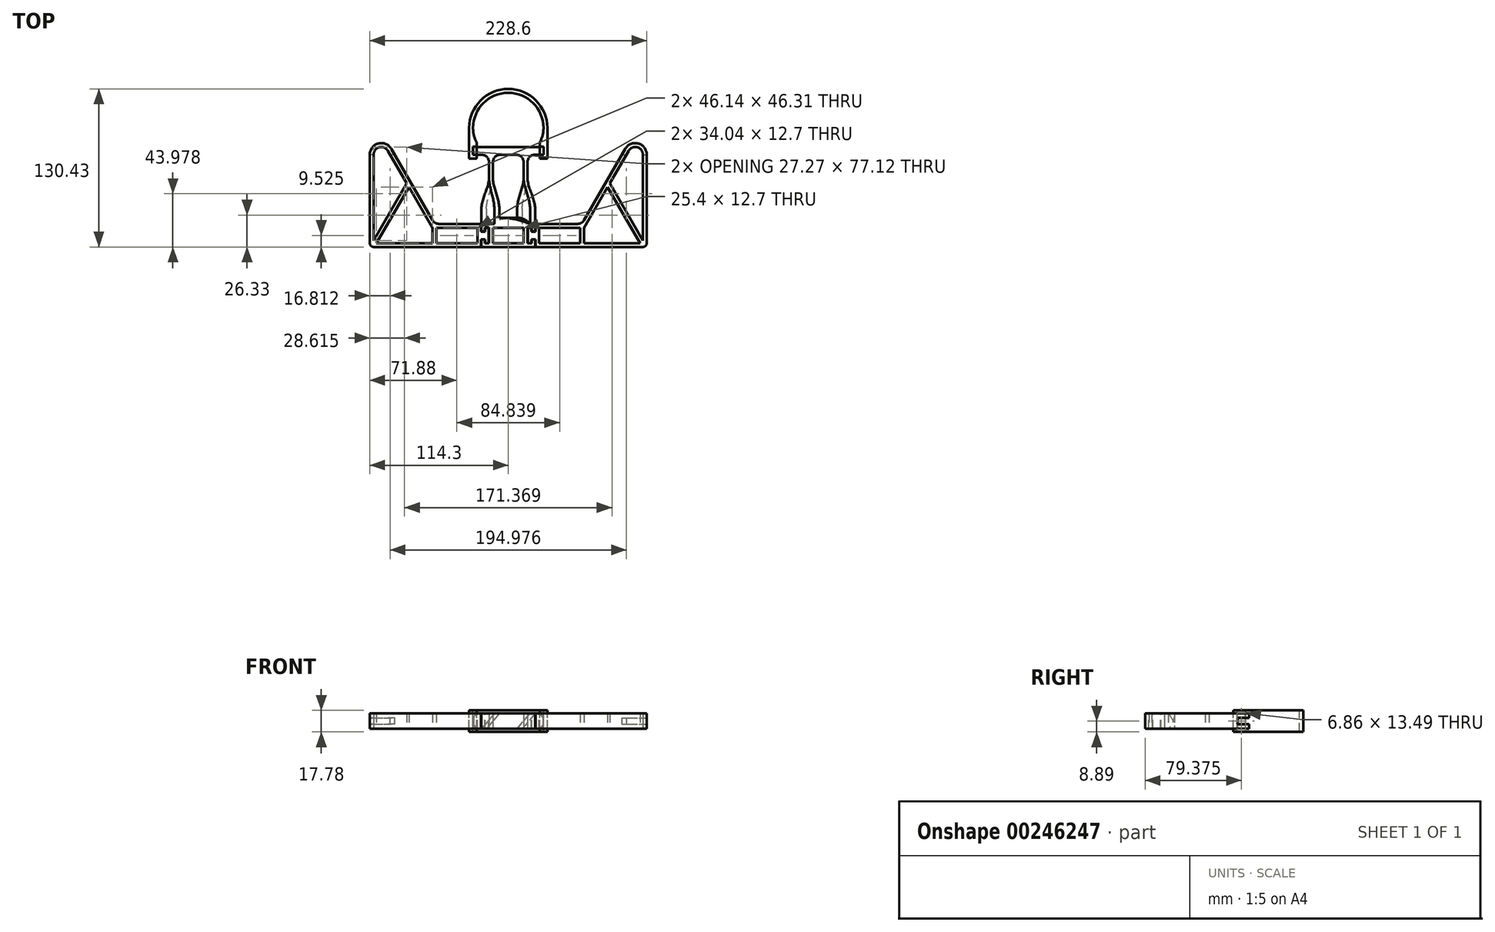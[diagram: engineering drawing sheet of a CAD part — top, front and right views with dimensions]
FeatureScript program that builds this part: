
annotation { "Feature Type Name" : "Feature", "Feature Type Description" : "" }
export const myFeature = defineFeature(function(context is Context, id is Id, definition is map)
    precondition{}
    {
        {
            var Q0;
            Q0=qCreatedBy(makeId("Top.planeOp"),FACE);
            var sketch = newSketch(context, id + "F0", { "sketchPlane" : qUnion([Q0])});
            skLineSegment(sketch, "E0", {"start": v(0, 0) * mm, "end": v(111.12, 0) * mm});
            skLineSegment(sketch, "E1", {"start": v(114.3, 3.18) * mm, "end": v(114.3, 76.2) * mm});
            skLineSegment(sketch, "E2", {"start": v(108.76, 3.18) * mm, "end": v(62.61, 3.18) * mm});
            skLineSegment(sketch, "E3", {"start": v(62.61, 3.18) * mm, "end": v(62.61, 15.88) * mm});
            skLineSegment(sketch, "E4", {"start": v(60.78, 19.05) * mm, "end": v(15.88, 19.05) * mm});
            skLineSegment(sketch, "E5", {"start": v(15.88, 19.05) * mm, "end": v(15.88, 76.2) * mm});
            skLineSegment(sketch, "E6", {"start": v(15.87, 76.2) * mm, "end": v(28.58, 76.2) * mm});
            skLineSegment(sketch, "E7", {"start": v(28.58, 76.2) * mm, "end": v(28.58, 82.55) * mm});
            skLineSegment(sketch, "E8", {"start": v(28.58, 82.55) * mm, "end": v(-28.58, 82.55) * mm});
            skLineSegment(sketch, "E9", {"start": v(-28.58, 82.55) * mm, "end": v(-28.58, 76.2) * mm});
            skLineSegment(sketch, "E10", {"start": v(-28.58, 76.2) * mm, "end": v(-15.87, 76.2) * mm});
            skLineSegment(sketch, "E11", {"start": v(-15.87, 76.2) * mm, "end": v(-15.88, 19.05) * mm});
            skLineSegment(sketch, "E12.bottom", {"start": v(59.44, 15.88) * mm, "end": v(0, 15.88) * mm});
            skLineSegment(sketch, "E12.top", {"start": v(59.44, 3.18) * mm, "end": v(0, 3.18) * mm});
            skLineSegment(sketch, "E12.left", {"start": v(59.44, 15.88) * mm, "end": v(59.44, 3.18) * mm});
            skPoint(sketch, "E13", {"position": v(0, 82.55) * mm});
            skLineSegment(sketch, "E14", {"start": v(-15.88, 76.2) * mm, "end": v(15.87, 76.2) * mm, "construction": true});
            skPoint(sketch, "E15", {"position": v(0, 76.2) * mm});
            skArc(sketch, "E16", {"start": v(111.13, 76.2) * mm, "mid": v(106.42, 82.33) * mm, "end": v(99.28, 79.38) * mm});
            skLineSegment(sketch, "E17", {"start": v(111.13, 5.42) * mm, "end": v(111.13, 76.2) * mm});
            skPoint(sketch, "E18.visualSharp", {"position": v(111.13, 3.18) * mm});
            skPoint(sketch, "E19.visualSharp", {"position": v(114.3, 0) * mm});
            skArc(sketch, "E19.filletArc", {"start": v(111.13, 0) * mm, "mid": v(113.37, 0.93) * mm, "end": v(114.3, 3.18) * mm});
            skLineSegment(sketch, "E20", {"start": v(108.76, 3.17) * mm, "end": v(82.02, 49.48) * mm});
            skLineSegment(sketch, "E21", {"start": v(111.13, 5.42) * mm, "end": v(83.85, 52.66) * mm});
            skLineSegment(sketch, "E22", {"start": v(0, 3.18) * mm, "end": v(0, 15.88) * mm, "construction": true});
            skArc(sketch, "E23", {"start": v(114.3, 76.2) * mm, "mid": v(107.24, 85.4) * mm, "end": v(96.53, 80.96) * mm});
            skLineSegment(sketch, "E24", {"start": v(96.53, 80.96) * mm, "end": v(60.78, 19.05) * mm});
            skLineSegment(sketch, "E25", {"start": v(99.28, 79.38) * mm, "end": v(83.85, 52.66) * mm});
            skLineSegment(sketch, "E26.trimOffspring", {"start": v(82.02, 49.48) * mm, "end": v(62.61, 15.88) * mm});
            skLineSegment(sketch, "E27.bottom", {"start": v(12.7, 19.05) * mm, "end": v(-12.7, 19.05) * mm});
            skLineSegment(sketch, "E27.top", {"start": v(12.7, 76.2) * mm, "end": v(-12.7, 76.2) * mm});
            skLineSegment(sketch, "E27.left", {"start": v(12.7, 19.05) * mm, "end": v(12.7, 76.2) * mm});
            skLineSegment(sketch, "E27.right", {"start": v(-12.7, 19.05) * mm, "end": v(-12.7, 76.2) * mm});
            skLineSegment(sketch, "E28.MirrorCS", {"start": v(-60.78, 19.05) * mm, "end": v(-15.88, 19.05) * mm});
            skLineSegment(sketch, "E29.MirrorCS", {"start": v(-59.44, 15.88) * mm, "end": v(0, 15.88) * mm});
            skLineSegment(sketch, "E30.MirrorCS", {"start": v(-59.44, 3.18) * mm, "end": v(0, 3.18) * mm});
            skLineSegment(sketch, "E31.MirrorCS", {"start": v(0, 0) * mm, "end": v(-111.12, 0) * mm});
            skLineSegment(sketch, "E32.MirrorCS", {"start": v(-59.44, 15.88) * mm, "end": v(-59.44, 3.18) * mm});
            skLineSegment(sketch, "E33.MirrorCS", {"start": v(-62.61, 3.18) * mm, "end": v(-62.61, 15.88) * mm});
            skLineSegment(sketch, "E34.MirrorCS", {"start": v(-82.02, 49.48) * mm, "end": v(-62.61, 15.88) * mm});
            skLineSegment(sketch, "E35.MirrorCS", {"start": v(-96.53, 80.96) * mm, "end": v(-60.78, 19.05) * mm});
            skArc(sketch, "E36.MirrorCS", {"start": v(-114.3, 76.2) * mm, "mid": v(-107.24, 85.4) * mm, "end": v(-96.53, 80.96) * mm});
            skArc(sketch, "E37.MirrorCS", {"start": v(-111.13, 76.2) * mm, "mid": v(-106.42, 82.33) * mm, "end": v(-99.28, 79.38) * mm});
            skLineSegment(sketch, "E38.MirrorCS", {"start": v(-99.28, 79.38) * mm, "end": v(-83.85, 52.66) * mm});
            skLineSegment(sketch, "E39.MirrorCS", {"start": v(-111.13, 5.42) * mm, "end": v(-83.85, 52.66) * mm});
            skLineSegment(sketch, "E40.MirrorCS", {"start": v(-108.76, 3.17) * mm, "end": v(-82.02, 49.48) * mm});
            skArc(sketch, "E41.MirrorCS", {"start": v(-111.13, 0) * mm, "mid": v(-113.37, 0.93) * mm, "end": v(-114.3, 3.18) * mm});
            skLineSegment(sketch, "E42.MirrorCS", {"start": v(-114.3, 3.18) * mm, "end": v(-114.3, 76.2) * mm});
            skLineSegment(sketch, "E43.MirrorCS", {"start": v(-111.13, 5.42) * mm, "end": v(-111.13, 76.2) * mm});
            skLineSegment(sketch, "E44.MirrorCS", {"start": v(-108.76, 3.18) * mm, "end": v(-62.61, 3.18) * mm});
            skSolve(sketch);
        }
        {
            var Q0;
            Q0=makeQuery(id+"F0.imprint","IMPRINT",FACE,{"disambiguationData":[TD([[makeQuery(id+"F0.imprint","IMPRINT",EDGE,{"derivedFrom":sQuery(id+"F0.wireOp",EDGE,"E0")}),1.0]])]});
            extrude(context, id + "F1", {"entities" : qUnion([Q0]), "depth" : 12.7 * mm});
        }
        {
            var Q0;
            Q0=makeQuery(id+"F1.opExtrude","CAP_EDGE",EDGE,{"disambiguationData":[OSD([sQuery(id+"F0.wireOp",EDGE,"E7")])],"isStart":true});
            var Q1;
            Q1=makeQuery(id+"F1.opExtrude","CAP_EDGE",EDGE,{"disambiguationData":[OSD([sQuery(id+"F0.wireOp",EDGE,"E7")])],"isStart":false});
            chamfer(context, id + "F2", {"entities" : qUnion([Q0, Q1]), "chamferType" : ChamferType.OFFSET_ANGLE, "width" : 3.17 * mm, "oppositeDirection" : false, "angle" : 40 * degree, "tangentPropagation" : true});
        }
        {
            var Q0;
            Q0=makeQuery(id+"F1.opExtrude","CAP_EDGE",EDGE,{"disambiguationData":[OSD([sQuery(id+"F0.wireOp",EDGE,"E9")])],"isStart":false});
            var Q1;
            Q1=makeQuery(id+"F1.opExtrude","CAP_EDGE",EDGE,{"disambiguationData":[OSD([sQuery(id+"F0.wireOp",EDGE,"E9")])],"isStart":true});
            chamfer(context, id + "F3", {"entities" : qUnion([Q0, Q1]), "chamferType" : ChamferType.OFFSET_ANGLE, "width" : 3.17 * mm, "oppositeDirection" : true, "angle" : 40 * degree, "tangentPropagation" : true});
        }
        {
            var Q0;
            Q0=makeQuery(id+"F1.opExtrude","SWEPT_EDGE",EDGE,{"disambiguationData":[OSD([sQuery(id+"F0.wireOp",EDGE,"E4"),sQuery(id+"F0.wireOp",EDGE,"E24")])]});
            var Q1;
            Q1=makeQuery(id+"F1.opExtrude","SWEPT_EDGE",EDGE,{"disambiguationData":[OSD([sQuery(id+"F0.wireOp",EDGE,"E5"),sQuery(id+"F0.wireOp",EDGE,"E6")])]});
            var Q2;
            Q2=makeQuery(id+"F1.opExtrude","SWEPT_EDGE",EDGE,{"disambiguationData":[OSD([sQuery(id+"F0.wireOp",EDGE,"E10"),sQuery(id+"F0.wireOp",EDGE,"E11")])]});
            var Q3;
            Q3=makeQuery(id+"F1.opExtrude","SWEPT_EDGE",EDGE,{"disambiguationData":[OSD([sQuery(id+"F0.wireOp",EDGE,"E28.MirrorCS"),sQuery(id+"F0.wireOp",EDGE,"E35.MirrorCS")])]});
            var Q4;
            Q4=makeQuery(id+"F1.opExtrude","SWEPT_EDGE",EDGE,{"disambiguationData":[OSD([sQuery(id+"F0.wireOp",EDGE,"E27.top"),sQuery(id+"F0.wireOp",EDGE,"E27.left")])]});
            var Q5;
            Q5=makeQuery(id+"F1.opExtrude","SWEPT_EDGE",EDGE,{"disambiguationData":[OSD([sQuery(id+"F0.wireOp",EDGE,"E27.top"),sQuery(id+"F0.wireOp",EDGE,"E27.right")])]});
            fillet(context, id + "F4", {"entities" : qUnion([Q0, Q1, Q2, Q3, Q4, Q5]), "radius" : 6.35 * mm, "tangentPropagation" : true, "allowEdgeOverflow" : false});
        }
        {
            var Q0;
            Q0=makeQuery(id+"F1.opExtrude","CAP_FACE",FACE,{"disambiguationData":[OSD([sQuery(id+"F0.wireOp",EDGE,"E0"),sQuery(id+"F0.wireOp",EDGE,"E1"),sQuery(id+"F0.wireOp",EDGE,"E2"),sQuery(id+"F0.wireOp",EDGE,"E3"),sQuery(id+"F0.wireOp",EDGE,"E4"),sQuery(id+"F0.wireOp",EDGE,"E5"),sQuery(id+"F0.wireOp",EDGE,"E6"),sQuery(id+"F0.wireOp",EDGE,"E7"),sQuery(id+"F0.wireOp",EDGE,"E8"),sQuery(id+"F0.wireOp",EDGE,"E9"),sQuery(id+"F0.wireOp",EDGE,"E10"),sQuery(id+"F0.wireOp",EDGE,"E11"),sQuery(id+"F0.wireOp",EDGE,"E12.bottom"),sQuery(id+"F0.wireOp",EDGE,"E12.top"),sQuery(id+"F0.wireOp",EDGE,"E12.left"),sQuery(id+"F0.wireOp",EDGE,"E16"),sQuery(id+"F0.wireOp",EDGE,"E17"),sQuery(id+"F0.wireOp",EDGE,"E19.filletArc"),sQuery(id+"F0.wireOp",EDGE,"E20"),sQuery(id+"F0.wireOp",EDGE,"E21"),sQuery(id+"F0.wireOp",EDGE,"E23"),sQuery(id+"F0.wireOp",EDGE,"E24"),sQuery(id+"F0.wireOp",EDGE,"E25"),sQuery(id+"F0.wireOp",EDGE,"E26.trimOffspring"),sQuery(id+"F0.wireOp",EDGE,"E27.bottom"),sQuery(id+"F0.wireOp",EDGE,"E27.top"),sQuery(id+"F0.wireOp",EDGE,"E27.left"),sQuery(id+"F0.wireOp",EDGE,"E27.right"),sQuery(id+"F0.wireOp",EDGE,"E28.MirrorCS"),sQuery(id+"F0.wireOp",EDGE,"E29.MirrorCS"),sQuery(id+"F0.wireOp",EDGE,"E30.MirrorCS"),sQuery(id+"F0.wireOp",EDGE,"E31.MirrorCS"),sQuery(id+"F0.wireOp",EDGE,"E32.MirrorCS"),sQuery(id+"F0.wireOp",EDGE,"E33.MirrorCS"),sQuery(id+"F0.wireOp",EDGE,"E34.MirrorCS"),sQuery(id+"F0.wireOp",EDGE,"E35.MirrorCS"),sQuery(id+"F0.wireOp",EDGE,"E36.MirrorCS"),sQuery(id+"F0.wireOp",EDGE,"E37.MirrorCS"),sQuery(id+"F0.wireOp",EDGE,"E38.MirrorCS"),sQuery(id+"F0.wireOp",EDGE,"E39.MirrorCS"),sQuery(id+"F0.wireOp",EDGE,"E40.MirrorCS"),sQuery(id+"F0.wireOp",EDGE,"E41.MirrorCS"),sQuery(id+"F0.wireOp",EDGE,"E42.MirrorCS"),sQuery(id+"F0.wireOp",EDGE,"E43.MirrorCS"),sQuery(id+"F0.wireOp",EDGE,"E44.MirrorCS")])],"isStart":false});
            var sketch = newSketch(context, id + "F5", { "sketchPlane" : qUnion([Q0])});
            skLineSegment(sketch, "E45.bottom", {"start": v(-25.4, 19.05) * mm, "end": v(-9.53, 19.05) * mm});
            skLineSegment(sketch, "E45.top", {"start": v(-25.4, 0) * mm, "end": v(-9.53, 0) * mm});
            skLineSegment(sketch, "E45.left", {"start": v(-25.4, 19.05) * mm, "end": v(-25.4, 0) * mm});
            skLineSegment(sketch, "E45.right", {"start": v(-9.53, 19.05) * mm, "end": v(-9.53, 0) * mm});
            skLineSegment(sketch, "E46.bottom", {"start": v(25.4, 19.05) * mm, "end": v(9.52, 19.05) * mm});
            skLineSegment(sketch, "E46.top", {"start": v(25.4, 0) * mm, "end": v(9.53, 0) * mm});
            skLineSegment(sketch, "E46.left", {"start": v(25.4, 19.05) * mm, "end": v(25.4, 0) * mm});
            skLineSegment(sketch, "E46.right", {"start": v(9.52, 19.05) * mm, "end": v(9.53, 0) * mm});
            skSolve(sketch);
        }
        {
            var Q0;
            {var subQ0=sQuery(id+"F5.wireOp",EDGE,"E45.left");var subQ1=makeQuery(id+"F1.opExtrude","CAP_EDGE",EDGE,{"disambiguationData":[OSD([sQuery(id+"F0.wireOp",EDGE,"E12.bottom"),sQuery(id+"F0.wireOp",EDGE,"E29.MirrorCS")])],"isStart":false});var subQ2=makeQuery(id+"F5.imprint","INTERSECT",VERTEX,{"derivedFrom":[subQ1,subQ0]});Q0=makeQuery(id+"F5.imprint","IMPRINT",FACE,{"disambiguationData":[TD([[makeQuery(id+"F5.imprint","IMPRINT",EDGE,{"disambiguationData":[TD([[subQ2,-1.0]])],"derivedFrom":subQ0}),1.0]])]});}
            var Q1;
            {var subQ0=sQuery(id+"F5.wireOp",EDGE,"E46.left");var subQ1=makeQuery(id+"F1.opExtrude","CAP_EDGE",EDGE,{"disambiguationData":[OSD([sQuery(id+"F0.wireOp",EDGE,"E12.bottom"),sQuery(id+"F0.wireOp",EDGE,"E29.MirrorCS")])],"isStart":false});var subQ2=makeQuery(id+"F5.imprint","INTERSECT",VERTEX,{"derivedFrom":[subQ1,subQ0]});Q1=makeQuery(id+"F5.imprint","IMPRINT",FACE,{"disambiguationData":[TD([[makeQuery(id+"F5.imprint","IMPRINT",EDGE,{"disambiguationData":[TD([[subQ2,-1.0]])],"derivedFrom":subQ0}),-1.0]])]});}
            var Q2;
            {var subQ0=sQuery(id+"F5.wireOp",EDGE,"E45.right");var subQ1=makeQuery(id+"F1.opExtrude","CAP_EDGE",EDGE,{"disambiguationData":[OSD([sQuery(id+"F0.wireOp",EDGE,"E12.bottom"),sQuery(id+"F0.wireOp",EDGE,"E29.MirrorCS")])],"isStart":false});var subQ2=makeQuery(id+"F5.imprint","INTERSECT",VERTEX,{"derivedFrom":[subQ1,subQ0]});Q2=makeQuery(id+"F5.imprint","IMPRINT",FACE,{"disambiguationData":[TD([[makeQuery(id+"F5.imprint","IMPRINT",EDGE,{"disambiguationData":[TD([[subQ2,-1.0]])],"derivedFrom":subQ0}),1.0]])]});}
            var Q3;
            Q3=makeQuery(id+"F1.opExtrude","CAP_FACE",FACE,{"disambiguationData":[OSD([sQuery(id+"F0.wireOp",EDGE,"E0"),sQuery(id+"F0.wireOp",EDGE,"E1"),sQuery(id+"F0.wireOp",EDGE,"E2"),sQuery(id+"F0.wireOp",EDGE,"E3"),sQuery(id+"F0.wireOp",EDGE,"E4"),sQuery(id+"F0.wireOp",EDGE,"E5"),sQuery(id+"F0.wireOp",EDGE,"E6"),sQuery(id+"F0.wireOp",EDGE,"E7"),sQuery(id+"F0.wireOp",EDGE,"E8"),sQuery(id+"F0.wireOp",EDGE,"E9"),sQuery(id+"F0.wireOp",EDGE,"E10"),sQuery(id+"F0.wireOp",EDGE,"E11"),sQuery(id+"F0.wireOp",EDGE,"E12.bottom"),sQuery(id+"F0.wireOp",EDGE,"E12.top"),sQuery(id+"F0.wireOp",EDGE,"E12.left"),sQuery(id+"F0.wireOp",EDGE,"E16"),sQuery(id+"F0.wireOp",EDGE,"E17"),sQuery(id+"F0.wireOp",EDGE,"E19.filletArc"),sQuery(id+"F0.wireOp",EDGE,"E20"),sQuery(id+"F0.wireOp",EDGE,"E21"),sQuery(id+"F0.wireOp",EDGE,"E23"),sQuery(id+"F0.wireOp",EDGE,"E24"),sQuery(id+"F0.wireOp",EDGE,"E25"),sQuery(id+"F0.wireOp",EDGE,"E26.trimOffspring"),sQuery(id+"F0.wireOp",EDGE,"E27.bottom"),sQuery(id+"F0.wireOp",EDGE,"E27.top"),sQuery(id+"F0.wireOp",EDGE,"E27.left"),sQuery(id+"F0.wireOp",EDGE,"E27.right"),sQuery(id+"F0.wireOp",EDGE,"E28.MirrorCS"),sQuery(id+"F0.wireOp",EDGE,"E29.MirrorCS"),sQuery(id+"F0.wireOp",EDGE,"E30.MirrorCS"),sQuery(id+"F0.wireOp",EDGE,"E31.MirrorCS"),sQuery(id+"F0.wireOp",EDGE,"E32.MirrorCS"),sQuery(id+"F0.wireOp",EDGE,"E33.MirrorCS"),sQuery(id+"F0.wireOp",EDGE,"E34.MirrorCS"),sQuery(id+"F0.wireOp",EDGE,"E35.MirrorCS"),sQuery(id+"F0.wireOp",EDGE,"E36.MirrorCS"),sQuery(id+"F0.wireOp",EDGE,"E37.MirrorCS"),sQuery(id+"F0.wireOp",EDGE,"E38.MirrorCS"),sQuery(id+"F0.wireOp",EDGE,"E39.MirrorCS"),sQuery(id+"F0.wireOp",EDGE,"E40.MirrorCS"),sQuery(id+"F0.wireOp",EDGE,"E41.MirrorCS"),sQuery(id+"F0.wireOp",EDGE,"E42.MirrorCS"),sQuery(id+"F0.wireOp",EDGE,"E43.MirrorCS"),sQuery(id+"F0.wireOp",EDGE,"E44.MirrorCS")])],"isStart":true});
            extrude(context, id + "F6", {"entities" : qUnion([Q0, Q1, Q2]), "operationType" : NewBodyOperationType.ADD, "endBound" : BoundingType.UP_TO_SURFACE, "oppositeDirection" : true, "endBoundEntityFace" : qUnion([Q3]), "depth" : 25.4 * mm});
        }
        {
            var Q0;
            {var subQ0=sQuery(id+"F0.wireOp",EDGE,"E30.MirrorCS");var subQ1=sQuery(id+"F0.wireOp",EDGE,"E29.MirrorCS");var subQ2=sQuery(id+"F0.wireOp",EDGE,"E12.top");var subQ3=sQuery(id+"F0.wireOp",EDGE,"E12.bottom");Q0=makeQuery(id+"F6.boolean.opBoolean","MERGE",FACE,{"derivedFrom":[makeQuery(id+"F1.opExtrude","CAP_FACE",FACE,{"disambiguationData":[OSD([sQuery(id+"F0.wireOp",EDGE,"E0"),sQuery(id+"F0.wireOp",EDGE,"E1"),sQuery(id+"F0.wireOp",EDGE,"E2"),sQuery(id+"F0.wireOp",EDGE,"E3"),sQuery(id+"F0.wireOp",EDGE,"E4"),sQuery(id+"F0.wireOp",EDGE,"E5"),sQuery(id+"F0.wireOp",EDGE,"E6"),sQuery(id+"F0.wireOp",EDGE,"E7"),sQuery(id+"F0.wireOp",EDGE,"E8"),sQuery(id+"F0.wireOp",EDGE,"E9"),sQuery(id+"F0.wireOp",EDGE,"E10"),sQuery(id+"F0.wireOp",EDGE,"E11"),subQ3,subQ2,sQuery(id+"F0.wireOp",EDGE,"E12.left"),sQuery(id+"F0.wireOp",EDGE,"E16"),sQuery(id+"F0.wireOp",EDGE,"E17"),sQuery(id+"F0.wireOp",EDGE,"E19.filletArc"),sQuery(id+"F0.wireOp",EDGE,"E20"),sQuery(id+"F0.wireOp",EDGE,"E21"),sQuery(id+"F0.wireOp",EDGE,"E23"),sQuery(id+"F0.wireOp",EDGE,"E24"),sQuery(id+"F0.wireOp",EDGE,"E25"),sQuery(id+"F0.wireOp",EDGE,"E26.trimOffspring"),sQuery(id+"F0.wireOp",EDGE,"E27.bottom"),sQuery(id+"F0.wireOp",EDGE,"E27.top"),sQuery(id+"F0.wireOp",EDGE,"E27.left"),sQuery(id+"F0.wireOp",EDGE,"E27.right"),sQuery(id+"F0.wireOp",EDGE,"E28.MirrorCS"),subQ1,subQ0,sQuery(id+"F0.wireOp",EDGE,"E31.MirrorCS"),sQuery(id+"F0.wireOp",EDGE,"E32.MirrorCS"),sQuery(id+"F0.wireOp",EDGE,"E33.MirrorCS"),sQuery(id+"F0.wireOp",EDGE,"E34.MirrorCS"),sQuery(id+"F0.wireOp",EDGE,"E35.MirrorCS"),sQuery(id+"F0.wireOp",EDGE,"E36.MirrorCS"),sQuery(id+"F0.wireOp",EDGE,"E37.MirrorCS"),sQuery(id+"F0.wireOp",EDGE,"E38.MirrorCS"),sQuery(id+"F0.wireOp",EDGE,"E39.MirrorCS"),sQuery(id+"F0.wireOp",EDGE,"E40.MirrorCS"),sQuery(id+"F0.wireOp",EDGE,"E41.MirrorCS"),sQuery(id+"F0.wireOp",EDGE,"E42.MirrorCS"),sQuery(id+"F0.wireOp",EDGE,"E43.MirrorCS"),sQuery(id+"F0.wireOp",EDGE,"E44.MirrorCS")])],"isStart":false}),makeQuery(id+"F6.opExtrude","CAP_FACE",FACE,{"disambiguationData":[OSD([subQ3,subQ2,subQ1,subQ0,sQuery(id+"F5.wireOp",EDGE,"E45.left"),sQuery(id+"F5.wireOp",EDGE,"E46.left")])],"isStart":true})]});}
            var sketch = newSketch(context, id + "F7", { "sketchPlane" : qUnion([Q0])});
            skLineSegment(sketch, "E47", {"start": v(-22.43, 19.05) * mm, "end": v(-22.43, 12.7) * mm});
            skLineSegment(sketch, "E48", {"start": v(-22.43, 12.7) * mm, "end": v(-19.05, 12.7) * mm});
            skLineSegment(sketch, "E49", {"start": v(-19.05, 12.7) * mm, "end": v(-19.05, 15.87) * mm});
            skLineSegment(sketch, "E50", {"start": v(-19.05, 15.88) * mm, "end": v(-16.08, 15.88) * mm});
            skLineSegment(sketch, "E51", {"start": v(-16.08, 15.87) * mm, "end": v(-16.08, 3.17) * mm});
            skLineSegment(sketch, "E52", {"start": v(-16.08, 3.17) * mm, "end": v(-19.05, 3.17) * mm});
            skLineSegment(sketch, "E53", {"start": v(-19.05, 3.17) * mm, "end": v(-19.05, 6.35) * mm});
            skLineSegment(sketch, "E54", {"start": v(-19.05, 6.35) * mm, "end": v(-22.43, 6.35) * mm});
            skLineSegment(sketch, "E55", {"start": v(-22.43, 6.35) * mm, "end": v(-22.43, 0) * mm});
            skLineSegment(sketch, "E56.0", {"start": v(-22.23, 6.15) * mm, "end": v(-22.22, 0) * mm});
            skLineSegment(sketch, "E56.1", {"start": v(-19.25, 6.15) * mm, "end": v(-22.23, 6.15) * mm});
            skLineSegment(sketch, "E56.2", {"start": v(-19.25, 2.97) * mm, "end": v(-19.25, 6.15) * mm});
            skLineSegment(sketch, "E56.3", {"start": v(-15.87, 2.97) * mm, "end": v(-19.25, 2.97) * mm});
            skLineSegment(sketch, "E56.4", {"start": v(-15.87, 16.08) * mm, "end": v(-15.87, 2.97) * mm});
            skLineSegment(sketch, "E56.5", {"start": v(-22.22, 19.05) * mm, "end": v(-22.22, 12.9) * mm});
            skLineSegment(sketch, "E56.6", {"start": v(-22.22, 12.9) * mm, "end": v(-19.25, 12.9) * mm});
            skLineSegment(sketch, "E56.7", {"start": v(-19.25, 12.9) * mm, "end": v(-19.25, 16.08) * mm});
            skLineSegment(sketch, "E56.8", {"start": v(-19.25, 16.08) * mm, "end": v(-15.87, 16.08) * mm});
            skLineSegment(sketch, "E57", {"start": v(0, 19.05) * mm, "end": v(0, 0) * mm, "construction": true});
            skLineSegment(sketch, "E58.MirrorCS", {"start": v(16.08, 15.88) * mm, "end": v(16.08, 3.18) * mm});
            skLineSegment(sketch, "E59.MirrorCS", {"start": v(15.87, 16.08) * mm, "end": v(15.88, 2.97) * mm});
            skLineSegment(sketch, "E60.MirrorCS", {"start": v(19.25, 16.08) * mm, "end": v(15.87, 16.08) * mm});
            skLineSegment(sketch, "E61.MirrorCS", {"start": v(19.05, 15.88) * mm, "end": v(16.08, 15.88) * mm});
            skLineSegment(sketch, "E62.MirrorCS", {"start": v(19.25, 12.9) * mm, "end": v(19.25, 16.08) * mm});
            skLineSegment(sketch, "E63.MirrorCS", {"start": v(19.05, 12.7) * mm, "end": v(19.05, 15.88) * mm});
            skLineSegment(sketch, "E64.MirrorCS", {"start": v(22.22, 19.05) * mm, "end": v(22.22, 12.9) * mm});
            skLineSegment(sketch, "E65.MirrorCS", {"start": v(22.22, 12.9) * mm, "end": v(19.25, 12.9) * mm});
            skLineSegment(sketch, "E66.MirrorCS", {"start": v(22.43, 12.7) * mm, "end": v(19.05, 12.7) * mm});
            skLineSegment(sketch, "E67.MirrorCS", {"start": v(22.43, 19.05) * mm, "end": v(22.43, 12.7) * mm});
            skLineSegment(sketch, "E68.MirrorCS", {"start": v(19.25, 2.97) * mm, "end": v(19.25, 6.15) * mm});
            skLineSegment(sketch, "E69.MirrorCS", {"start": v(19.25, 6.15) * mm, "end": v(22.23, 6.15) * mm});
            skLineSegment(sketch, "E70.MirrorCS", {"start": v(22.23, 6.15) * mm, "end": v(22.23, 0) * mm});
            skLineSegment(sketch, "E71.MirrorCS", {"start": v(22.43, 6.35) * mm, "end": v(22.43, 0) * mm});
            skLineSegment(sketch, "E72.MirrorCS", {"start": v(19.05, 6.35) * mm, "end": v(22.43, 6.35) * mm});
            skLineSegment(sketch, "E73.MirrorCS", {"start": v(19.05, 3.18) * mm, "end": v(19.05, 6.35) * mm});
            skLineSegment(sketch, "E74.MirrorCS", {"start": v(16.08, 3.17) * mm, "end": v(19.05, 3.17) * mm});
            skLineSegment(sketch, "E75.MirrorCS", {"start": v(15.87, 2.97) * mm, "end": v(19.25, 2.97) * mm});
            skLineSegment(sketch, "E76.bottom", {"start": v(-12.7, 3.18) * mm, "end": v(12.7, 3.18) * mm});
            skLineSegment(sketch, "E76.top", {"start": v(-12.7, 15.88) * mm, "end": v(12.7, 15.88) * mm});
            skLineSegment(sketch, "E76.left", {"start": v(-12.7, 3.17) * mm, "end": v(-12.7, 15.88) * mm});
            skLineSegment(sketch, "E76.right", {"start": v(12.7, 3.18) * mm, "end": v(12.7, 15.88) * mm});
            skPoint(sketch, "E77", {"position": v(0, 15.88) * mm});
            skSolve(sketch);
        }
        {
            var Q0;
            Q0=makeQuery(id+"F7.imprint","IMPRINT",FACE,{"disambiguationData":[TD([[makeQuery(id+"F7.imprint","IMPRINT",EDGE,{"derivedFrom":sQuery(id+"F7.wireOp",EDGE,"E47")}),1.0]])]});
            var Q1;
            Q1=makeQuery(id+"F7.imprint","IMPRINT",FACE,{"disambiguationData":[TD([[makeQuery(id+"F7.imprint","IMPRINT",EDGE,{"derivedFrom":sQuery(id+"F7.wireOp",EDGE,"E76.bottom")}),1.0]])]});
            var Q2;
            Q2=makeQuery(id+"F7.imprint","IMPRINT",FACE,{"disambiguationData":[TD([[makeQuery(id+"F7.imprint","IMPRINT",EDGE,{"derivedFrom":sQuery(id+"F7.wireOp",EDGE,"E58.MirrorCS")}),-1.0]])]});
            var Q3;
            {var subQ0=sQuery(id+"F0.wireOp",EDGE,"E44.MirrorCS");var subQ1=sQuery(id+"F0.wireOp",EDGE,"E43.MirrorCS");var subQ2=sQuery(id+"F0.wireOp",EDGE,"E42.MirrorCS");var subQ3=sQuery(id+"F0.wireOp",EDGE,"E41.MirrorCS");var subQ4=sQuery(id+"F0.wireOp",EDGE,"E40.MirrorCS");var subQ5=sQuery(id+"F0.wireOp",EDGE,"E39.MirrorCS");var subQ6=sQuery(id+"F0.wireOp",EDGE,"E38.MirrorCS");var subQ7=sQuery(id+"F0.wireOp",EDGE,"E37.MirrorCS");var subQ8=sQuery(id+"F0.wireOp",EDGE,"E36.MirrorCS");var subQ9=sQuery(id+"F0.wireOp",EDGE,"E35.MirrorCS");var subQ10=sQuery(id+"F0.wireOp",EDGE,"E34.MirrorCS");var subQ11=sQuery(id+"F0.wireOp",EDGE,"E33.MirrorCS");var subQ12=sQuery(id+"F0.wireOp",EDGE,"E32.MirrorCS");var subQ13=sQuery(id+"F0.wireOp",EDGE,"E31.MirrorCS");var subQ14=sQuery(id+"F0.wireOp",EDGE,"E30.MirrorCS");var subQ15=sQuery(id+"F0.wireOp",EDGE,"E29.MirrorCS");var subQ16=sQuery(id+"F0.wireOp",EDGE,"E28.MirrorCS");var subQ17=sQuery(id+"F0.wireOp",EDGE,"E27.right");var subQ18=sQuery(id+"F0.wireOp",EDGE,"E27.left");var subQ19=sQuery(id+"F0.wireOp",EDGE,"E27.top");var subQ20=sQuery(id+"F0.wireOp",EDGE,"E27.bottom");var subQ21=sQuery(id+"F0.wireOp",EDGE,"E26.trimOffspring");var subQ22=sQuery(id+"F0.wireOp",EDGE,"E25");var subQ23=sQuery(id+"F0.wireOp",EDGE,"E24");var subQ24=sQuery(id+"F0.wireOp",EDGE,"E23");var subQ25=sQuery(id+"F0.wireOp",EDGE,"E21");var subQ26=sQuery(id+"F0.wireOp",EDGE,"E20");var subQ27=sQuery(id+"F0.wireOp",EDGE,"E19.filletArc");var subQ28=sQuery(id+"F0.wireOp",EDGE,"E17");var subQ29=sQuery(id+"F0.wireOp",EDGE,"E16");var subQ30=sQuery(id+"F0.wireOp",EDGE,"E12.left");var subQ31=sQuery(id+"F0.wireOp",EDGE,"E12.top");var subQ32=sQuery(id+"F0.wireOp",EDGE,"E12.bottom");var subQ33=sQuery(id+"F0.wireOp",EDGE,"E11");var subQ34=sQuery(id+"F0.wireOp",EDGE,"E10");var subQ35=sQuery(id+"F0.wireOp",EDGE,"E9");var subQ36=sQuery(id+"F0.wireOp",EDGE,"E8");var subQ37=sQuery(id+"F0.wireOp",EDGE,"E7");var subQ38=sQuery(id+"F0.wireOp",EDGE,"E6");var subQ39=sQuery(id+"F0.wireOp",EDGE,"E5");var subQ40=sQuery(id+"F0.wireOp",EDGE,"E4");var subQ41=sQuery(id+"F0.wireOp",EDGE,"E3");var subQ42=sQuery(id+"F0.wireOp",EDGE,"E2");var subQ43=sQuery(id+"F0.wireOp",EDGE,"E1");var subQ44=sQuery(id+"F0.wireOp",EDGE,"E0");Q3=makeQuery(id+"F6.boolean.opBoolean","MERGE",FACE,{"derivedFrom":[makeQuery(id+"F1.opExtrude","CAP_FACE",FACE,{"disambiguationData":[OSD([subQ44,subQ43,subQ42,subQ41,subQ40,subQ39,subQ38,subQ37,subQ36,subQ35,subQ34,subQ33,subQ32,subQ31,subQ30,subQ29,subQ28,subQ27,subQ26,subQ25,subQ24,subQ23,subQ22,subQ21,subQ20,subQ19,subQ18,subQ17,subQ16,subQ15,subQ14,subQ13,subQ12,subQ11,subQ10,subQ9,subQ8,subQ7,subQ6,subQ5,subQ4,subQ3,subQ2,subQ1,subQ0])],"isStart":true}),makeQuery(id+"F6.opExtrude","CAP_FACE",FACE,{"disambiguationData":[OSD([subQ44,subQ43,subQ42,subQ41,subQ40,subQ39,subQ38,subQ37,subQ36,subQ35,subQ34,subQ33,subQ32,subQ31,subQ30,subQ29,subQ28,subQ27,subQ26,subQ25,subQ24,subQ23,subQ22,subQ21,subQ20,subQ19,subQ18,subQ17,subQ16,subQ15,subQ14,subQ13,subQ12,subQ11,subQ10,subQ9,subQ8,subQ7,subQ6,subQ5,subQ4,subQ3,subQ2,subQ1,subQ0])],"isStart":false})]});}
            extrude(context, id + "F8", {"entities" : qUnion([Q0, Q1, Q2]), "operationType" : NewBodyOperationType.REMOVE, "endBound" : BoundingType.UP_TO_SURFACE, "oppositeDirection" : true, "endBoundEntityFace" : qUnion([Q3]), "depth" : 25.4 * mm});
        }
        {
            var Q0;
            Q0=makeQuery(id+"F1.opExtrude","SWEPT_FACE",FACE,{"disambiguationData":[OSD([sQuery(id+"F0.wireOp",EDGE,"E27.bottom")])]});
            var sketch = newSketch(context, id + "F9", { "sketchPlane" : qUnion([Q0])});
            skLineSegment(sketch, "E78", {"start": v(-7.37, 0) * mm, "end": v(-18.03, 12.7) * mm});
            skLineSegment(sketch, "E79", {"start": v(7.37, 12.7) * mm, "end": v(18.03, 0) * mm});
            skPoint(sketch, "E80", {"position": v(-12.7, 6.35) * mm});
            skPoint(sketch, "E81", {"position": v(12.7, 6.35) * mm});
            skLineSegment(sketch, "E82", {"start": v(11.52, 12.7) * mm, "end": v(22.17, 0) * mm});
            skLineSegment(sketch, "E83", {"start": v(-22.17, 12.7) * mm, "end": v(-11.52, 0) * mm});
            skLineSegment(sketch, "E84", {"start": v(18.03, 0) * mm, "end": v(22.17, 0) * mm});
            skLineSegment(sketch, "E85", {"start": v(11.52, 12.7) * mm, "end": v(7.37, 12.7) * mm});
            skLineSegment(sketch, "E86", {"start": v(-18.03, 12.7) * mm, "end": v(-22.17, 12.7) * mm});
            skLineSegment(sketch, "E87", {"start": v(-7.37, 0) * mm, "end": v(-11.52, 0) * mm});
            skSolve(sketch);
        }
        {
            var Q0;
            {var subQ0=sQuery(id+"F0.wireOp",EDGE,"E27.top");var subQ1=sQuery(id+"F0.wireOp",EDGE,"E27.right");var subQ2=sQuery(id+"F0.wireOp",EDGE,"E27.left");var subQ3=sQuery(id+"F0.wireOp",EDGE,"E11");var subQ4=sQuery(id+"F0.wireOp",EDGE,"E10");var subQ5=sQuery(id+"F0.wireOp",EDGE,"E6");var subQ6=sQuery(id+"F0.wireOp",EDGE,"E5");var subQ7=sQuery(id+"F0.wireOp",EDGE,"E9");var subQ8=sQuery(id+"F0.wireOp",EDGE,"E7");var subQ9=sQuery(id+"F0.wireOp",EDGE,"E27.bottom");var subQ10=sQuery(id+"F0.wireOp",EDGE,"E31.MirrorCS");var subQ11=sQuery(id+"F0.wireOp",EDGE,"E0");var subQ12=sQuery(id+"F0.wireOp",EDGE,"E8");var subQ13=sQuery(id+"F0.wireOp",EDGE,"E44.MirrorCS");var subQ14=sQuery(id+"F0.wireOp",EDGE,"E43.MirrorCS");var subQ15=sQuery(id+"F0.wireOp",EDGE,"E42.MirrorCS");var subQ16=sQuery(id+"F0.wireOp",EDGE,"E41.MirrorCS");var subQ17=sQuery(id+"F0.wireOp",EDGE,"E40.MirrorCS");var subQ18=sQuery(id+"F0.wireOp",EDGE,"E39.MirrorCS");var subQ19=sQuery(id+"F0.wireOp",EDGE,"E38.MirrorCS");var subQ20=sQuery(id+"F0.wireOp",EDGE,"E37.MirrorCS");var subQ21=sQuery(id+"F0.wireOp",EDGE,"E36.MirrorCS");var subQ22=sQuery(id+"F0.wireOp",EDGE,"E35.MirrorCS");var subQ23=sQuery(id+"F0.wireOp",EDGE,"E34.MirrorCS");var subQ24=sQuery(id+"F0.wireOp",EDGE,"E33.MirrorCS");var subQ25=sQuery(id+"F0.wireOp",EDGE,"E32.MirrorCS");var subQ26=sQuery(id+"F0.wireOp",EDGE,"E30.MirrorCS");var subQ27=sQuery(id+"F0.wireOp",EDGE,"E29.MirrorCS");var subQ28=sQuery(id+"F0.wireOp",EDGE,"E28.MirrorCS");var subQ29=sQuery(id+"F0.wireOp",EDGE,"E26.trimOffspring");var subQ30=sQuery(id+"F0.wireOp",EDGE,"E25");var subQ31=sQuery(id+"F0.wireOp",EDGE,"E24");var subQ32=sQuery(id+"F0.wireOp",EDGE,"E23");var subQ33=sQuery(id+"F0.wireOp",EDGE,"E21");var subQ34=sQuery(id+"F0.wireOp",EDGE,"E20");var subQ35=sQuery(id+"F0.wireOp",EDGE,"E19.filletArc");var subQ36=sQuery(id+"F0.wireOp",EDGE,"E17");var subQ37=sQuery(id+"F0.wireOp",EDGE,"E16");var subQ38=sQuery(id+"F0.wireOp",EDGE,"E12.left");var subQ39=sQuery(id+"F0.wireOp",EDGE,"E12.top");var subQ40=sQuery(id+"F0.wireOp",EDGE,"E12.bottom");var subQ41=sQuery(id+"F0.wireOp",EDGE,"E4");var subQ42=sQuery(id+"F0.wireOp",EDGE,"E3");var subQ43=sQuery(id+"F0.wireOp",EDGE,"E2");var subQ44=sQuery(id+"F0.wireOp",EDGE,"E1");Q0=makeQuery(id+"F8.boolean.opBoolean","SPLIT",FACE,{"disambiguationData":[TD([makeQuery(id+"F1.opExtrude","SWEPT_FACE",FACE,{"disambiguationData":[OSD([subQ6])]})])],"derivedFrom":makeQuery(id+"F6.boolean.opBoolean","MERGE",FACE,{"derivedFrom":[makeQuery(id+"F1.opExtrude","CAP_FACE",FACE,{"disambiguationData":[OSD([subQ11,subQ44,subQ43,subQ42,subQ41,subQ6,subQ5,subQ8,subQ12,subQ7,subQ4,subQ3,subQ40,subQ39,subQ38,subQ37,subQ36,subQ35,subQ34,subQ33,subQ32,subQ31,subQ30,subQ29,subQ9,subQ0,subQ2,subQ1,subQ28,subQ27,subQ26,subQ10,subQ25,subQ24,subQ23,subQ22,subQ21,subQ20,subQ19,subQ18,subQ17,subQ16,subQ15,subQ14,subQ13])],"isStart":true}),makeQuery(id+"F6.opExtrude","CAP_FACE",FACE,{"disambiguationData":[OSD([subQ11,subQ44,subQ43,subQ42,subQ41,subQ6,subQ5,subQ8,subQ12,subQ7,subQ4,subQ3,subQ40,subQ39,subQ38,subQ37,subQ36,subQ35,subQ34,subQ33,subQ32,subQ31,subQ30,subQ29,subQ9,subQ0,subQ2,subQ1,subQ28,subQ27,subQ26,subQ10,subQ25,subQ24,subQ23,subQ22,subQ21,subQ20,subQ19,subQ18,subQ17,subQ16,subQ15,subQ14,subQ13])],"isStart":false})]})});}
            var sketch = newSketch(context, id + "F10", { "sketchPlane" : qUnion([Q0])});
            skLineSegment(sketch, "E88.bottom", {"start": v(-15.88, -19.05) * mm, "end": v(-12.7, -19.05) * mm});
            skLineSegment(sketch, "E88.top", {"start": v(-15.87, -57.15) * mm, "end": v(-12.7, -57.15) * mm});
            skLineSegment(sketch, "E88.left", {"start": v(-15.88, -19.05) * mm, "end": v(-15.88, -57.15) * mm});
            skLineSegment(sketch, "E88.right", {"start": v(-12.7, -19.05) * mm, "end": v(-12.7, -57.15) * mm});
            skLineSegment(sketch, "E89.bottom", {"start": v(15.88, -19.05) * mm, "end": v(12.7, -19.05) * mm});
            skLineSegment(sketch, "E89.top", {"start": v(15.88, -57.15) * mm, "end": v(12.7, -57.15) * mm});
            skLineSegment(sketch, "E89.left", {"start": v(15.88, -19.05) * mm, "end": v(15.88, -57.15) * mm});
            skLineSegment(sketch, "E89.right", {"start": v(12.7, -19.05) * mm, "end": v(12.7, -57.15) * mm});
            skSolve(sketch);
        }
        {
            var Q0;
            Q0=makeQuery(id+"F10.imprint","IMPRINT",FACE,{"disambiguationData":[TD([[makeQuery(id+"F10.imprint","IMPRINT",EDGE,{"derivedFrom":sQuery(id+"F10.wireOp",EDGE,"E88.bottom")}),-1.0]])]});
            var Q1;
            Q1=makeQuery(id+"F10.imprint","IMPRINT",FACE,{"disambiguationData":[TD([[makeQuery(id+"F10.imprint","IMPRINT",EDGE,{"derivedFrom":sQuery(id+"F10.wireOp",EDGE,"E89.bottom")}),1.0]])]});
            var Q2;
            {var subQ0=sQuery(id+"F0.wireOp",EDGE,"E27.top");var subQ1=sQuery(id+"F0.wireOp",EDGE,"E27.right");var subQ2=sQuery(id+"F0.wireOp",EDGE,"E27.left");var subQ3=sQuery(id+"F0.wireOp",EDGE,"E11");var subQ4=sQuery(id+"F0.wireOp",EDGE,"E10");var subQ5=sQuery(id+"F0.wireOp",EDGE,"E6");var subQ6=sQuery(id+"F0.wireOp",EDGE,"E5");var subQ7=sQuery(id+"F0.wireOp",EDGE,"E7");var subQ8=sQuery(id+"F0.wireOp",EDGE,"E27.bottom");var subQ9=sQuery(id+"F0.wireOp",EDGE,"E31.MirrorCS");var subQ10=sQuery(id+"F0.wireOp",EDGE,"E0");var subQ11=sQuery(id+"F0.wireOp",EDGE,"E9");var subQ12=sQuery(id+"F0.wireOp",EDGE,"E8");var subQ13=sQuery(id+"F0.wireOp",EDGE,"E30.MirrorCS");var subQ14=sQuery(id+"F0.wireOp",EDGE,"E29.MirrorCS");var subQ15=sQuery(id+"F0.wireOp",EDGE,"E12.top");var subQ16=sQuery(id+"F0.wireOp",EDGE,"E12.bottom");Q2=makeQuery(id+"F8.boolean.opBoolean","SPLIT",FACE,{"disambiguationData":[TD([makeQuery(id+"F1.opExtrude","SWEPT_FACE",FACE,{"disambiguationData":[OSD([subQ6])]})])],"derivedFrom":makeQuery(id+"F6.boolean.opBoolean","MERGE",FACE,{"derivedFrom":[makeQuery(id+"F1.opExtrude","CAP_FACE",FACE,{"disambiguationData":[OSD([subQ10,sQuery(id+"F0.wireOp",EDGE,"E1"),sQuery(id+"F0.wireOp",EDGE,"E2"),sQuery(id+"F0.wireOp",EDGE,"E3"),sQuery(id+"F0.wireOp",EDGE,"E4"),subQ6,subQ5,subQ7,subQ12,subQ11,subQ4,subQ3,subQ16,subQ15,sQuery(id+"F0.wireOp",EDGE,"E12.left"),sQuery(id+"F0.wireOp",EDGE,"E16"),sQuery(id+"F0.wireOp",EDGE,"E17"),sQuery(id+"F0.wireOp",EDGE,"E19.filletArc"),sQuery(id+"F0.wireOp",EDGE,"E20"),sQuery(id+"F0.wireOp",EDGE,"E21"),sQuery(id+"F0.wireOp",EDGE,"E23"),sQuery(id+"F0.wireOp",EDGE,"E24"),sQuery(id+"F0.wireOp",EDGE,"E25"),sQuery(id+"F0.wireOp",EDGE,"E26.trimOffspring"),subQ8,subQ0,subQ2,subQ1,sQuery(id+"F0.wireOp",EDGE,"E28.MirrorCS"),subQ14,subQ13,subQ9,sQuery(id+"F0.wireOp",EDGE,"E32.MirrorCS"),sQuery(id+"F0.wireOp",EDGE,"E33.MirrorCS"),sQuery(id+"F0.wireOp",EDGE,"E34.MirrorCS"),sQuery(id+"F0.wireOp",EDGE,"E35.MirrorCS"),sQuery(id+"F0.wireOp",EDGE,"E36.MirrorCS"),sQuery(id+"F0.wireOp",EDGE,"E37.MirrorCS"),sQuery(id+"F0.wireOp",EDGE,"E38.MirrorCS"),sQuery(id+"F0.wireOp",EDGE,"E39.MirrorCS"),sQuery(id+"F0.wireOp",EDGE,"E40.MirrorCS"),sQuery(id+"F0.wireOp",EDGE,"E41.MirrorCS"),sQuery(id+"F0.wireOp",EDGE,"E42.MirrorCS"),sQuery(id+"F0.wireOp",EDGE,"E43.MirrorCS"),sQuery(id+"F0.wireOp",EDGE,"E44.MirrorCS")])],"isStart":false}),makeQuery(id+"F6.opExtrude","CAP_FACE",FACE,{"disambiguationData":[OSD([subQ16,subQ15,subQ14,subQ13,sQuery(id+"F5.wireOp",EDGE,"E45.left"),sQuery(id+"F5.wireOp",EDGE,"E46.left")])],"isStart":true})]})});}
            extrude(context, id + "F11", {"entities" : qUnion([Q0, Q1]), "operationType" : NewBodyOperationType.REMOVE, "endBound" : BoundingType.UP_TO_SURFACE, "oppositeDirection" : true, "endBoundEntityFace" : qUnion([Q2]), "depth" : 25.4 * mm});
        }
        {
            var Q0;
            {var subQ0=sQuery(id+"F9.wireOp",EDGE,"E84");Q0=makeQuery(id+"F9.imprint","IMPRINT",FACE,{"disambiguationData":[TD([[makeQuery(id+"F9.imprint","IMPRINT",EDGE,{"derivedFrom":subQ0}),1.0]])]});}
            var Q1;
            {var subQ0=sQuery(id+"F9.wireOp",EDGE,"E85");Q1=makeQuery(id+"F9.imprint","IMPRINT",FACE,{"disambiguationData":[TD([[makeQuery(id+"F9.imprint","IMPRINT",EDGE,{"derivedFrom":subQ0}),-1.0]])]});}
            var Q2;
            {var subQ0=sQuery(id+"F9.wireOp",EDGE,"E87");Q2=makeQuery(id+"F9.imprint","IMPRINT",FACE,{"disambiguationData":[TD([[makeQuery(id+"F9.imprint","IMPRINT",EDGE,{"derivedFrom":subQ0}),1.0]])]});}
            var Q3;
            {var subQ0=sQuery(id+"F9.wireOp",EDGE,"E86");Q3=makeQuery(id+"F9.imprint","IMPRINT",FACE,{"disambiguationData":[TD([[makeQuery(id+"F9.imprint","IMPRINT",EDGE,{"derivedFrom":subQ0}),1.0]])]});}
            extrude(context, id + "F12", {"entities" : qUnion([Q0, Q1, Q2, Q3]), "operationType" : NewBodyOperationType.ADD, "depth" : 12.7 * mm});
        }
        {
            var Q2;
            Q2=makeQuery(id+"F12.opExtrude","CAP_FACE",FACE,{"disambiguationData":[OSD([sQuery(id+"F9.wireOp",EDGE,"E78"),sQuery(id+"F9.wireOp",EDGE,"E83"),sQuery(id+"F9.wireOp",EDGE,"E86"),sQuery(id+"F9.wireOp",EDGE,"E87")])],"isStart":false});
            var Q3;
            Q3=makeQuery(id+"F11.boolean.opBoolean","COPY",FACE,{"derivedFrom":makeQuery(id+"F11.opExtrude","SWEPT_FACE",FACE,{"disambiguationData":[OSD([sQuery(id+"F10.wireOp",EDGE,"E89.top")])]})});
            loft(context, id + "F13", {"operationType" : NewBodyOperationType.ADD, "startCondition" : LoftEndDerivativeType.NORMAL_TO_PROFILE, "startMagnitude" : 1, "endCondition" : LoftEndDerivativeType.NORMAL_TO_PROFILE, "endMagnitude" : 1, "sheetProfilesArray" : [{ "sheetProfileEntities" : qUnion([Q2]) }, { "sheetProfileEntities" : qUnion([Q3]) }]});
        }
        {
            var Q1;
            Q1=makeQuery(id+"F12.opExtrude","CAP_FACE",FACE,{"disambiguationData":[OSD([sQuery(id+"F9.wireOp",EDGE,"E79"),sQuery(id+"F9.wireOp",EDGE,"E82"),sQuery(id+"F9.wireOp",EDGE,"E84"),sQuery(id+"F9.wireOp",EDGE,"E85")])],"isStart":false});
            var Q2;
            Q2=makeQuery(id+"F11.boolean.opBoolean","COPY",FACE,{"derivedFrom":makeQuery(id+"F11.opExtrude","SWEPT_FACE",FACE,{"disambiguationData":[OSD([sQuery(id+"F10.wireOp",EDGE,"E88.top")])]})});
            loft(context, id + "F14", {"operationType" : NewBodyOperationType.ADD, "startCondition" : LoftEndDerivativeType.NORMAL_TO_PROFILE, "startMagnitude" : 1, "endCondition" : LoftEndDerivativeType.NORMAL_TO_PROFILE, "endMagnitude" : 1, "sheetProfilesArray" : [{ "sheetProfileEntities" : qUnion([Q1]) }, { "sheetProfileEntities" : qUnion([Q2]) }]});
        }
        {
            var Q0;
            {var subQ0=sQuery(id+"F10.wireOp",EDGE,"E88.top");var subQ1=sQuery(id+"F9.wireOp",EDGE,"E84");var subQ2=sQuery(id+"F0.wireOp",EDGE,"E27.right");var subQ3=sQuery(id+"F0.wireOp",EDGE,"E11");var subQ4=sQuery(id+"F10.wireOp",EDGE,"E89.top");var subQ5=sQuery(id+"F9.wireOp",EDGE,"E87");var subQ6=sQuery(id+"F0.wireOp",EDGE,"E27.left");var subQ7=sQuery(id+"F0.wireOp",EDGE,"E27.bottom");var subQ8=sQuery(id+"F0.wireOp",EDGE,"E5");var subQ20=makeQuery(id+"F1.opExtrude","SWEPT_FACE",FACE,{"disambiguationData":[OSD([subQ7])]});var subQ24=sQuery(id+"F0.wireOp",EDGE,"E31.MirrorCS");var subQ25=sQuery(id+"F0.wireOp",EDGE,"E0");var subQ37=sQuery(id+"F0.wireOp",EDGE,"E27.top");var subQ41=sQuery(id+"F0.wireOp",EDGE,"E10");var subQ43=sQuery(id+"F0.wireOp",EDGE,"E6");var subQ46=sQuery(id+"F0.wireOp",EDGE,"E9");var subQ49=sQuery(id+"F0.wireOp",EDGE,"E7");var subQ52=makeQuery(id+"F1.opExtrude","SWEPT_FACE",FACE,{"disambiguationData":[OSD([subQ8])]});var subQ55=sQuery(id+"F0.wireOp",EDGE,"E8");var subQ57=sQuery(id+"F0.wireOp",EDGE,"E44.MirrorCS");var subQ58=sQuery(id+"F0.wireOp",EDGE,"E43.MirrorCS");var subQ59=sQuery(id+"F0.wireOp",EDGE,"E42.MirrorCS");var subQ60=sQuery(id+"F0.wireOp",EDGE,"E41.MirrorCS");var subQ61=sQuery(id+"F0.wireOp",EDGE,"E40.MirrorCS");var subQ62=sQuery(id+"F0.wireOp",EDGE,"E39.MirrorCS");var subQ63=sQuery(id+"F0.wireOp",EDGE,"E38.MirrorCS");var subQ64=sQuery(id+"F0.wireOp",EDGE,"E37.MirrorCS");var subQ65=sQuery(id+"F0.wireOp",EDGE,"E36.MirrorCS");var subQ66=sQuery(id+"F0.wireOp",EDGE,"E35.MirrorCS");var subQ67=sQuery(id+"F0.wireOp",EDGE,"E34.MirrorCS");var subQ68=sQuery(id+"F0.wireOp",EDGE,"E33.MirrorCS");var subQ69=sQuery(id+"F0.wireOp",EDGE,"E32.MirrorCS");var subQ70=sQuery(id+"F0.wireOp",EDGE,"E30.MirrorCS");var subQ71=sQuery(id+"F0.wireOp",EDGE,"E29.MirrorCS");var subQ72=sQuery(id+"F0.wireOp",EDGE,"E28.MirrorCS");var subQ73=sQuery(id+"F0.wireOp",EDGE,"E26.trimOffspring");var subQ74=sQuery(id+"F0.wireOp",EDGE,"E25");var subQ75=sQuery(id+"F0.wireOp",EDGE,"E24");var subQ76=sQuery(id+"F0.wireOp",EDGE,"E23");var subQ77=sQuery(id+"F0.wireOp",EDGE,"E21");var subQ78=sQuery(id+"F0.wireOp",EDGE,"E20");var subQ79=sQuery(id+"F0.wireOp",EDGE,"E19.filletArc");var subQ80=sQuery(id+"F0.wireOp",EDGE,"E17");var subQ81=sQuery(id+"F0.wireOp",EDGE,"E16");var subQ82=sQuery(id+"F0.wireOp",EDGE,"E12.left");var subQ83=sQuery(id+"F0.wireOp",EDGE,"E12.top");var subQ84=sQuery(id+"F0.wireOp",EDGE,"E12.bottom");var subQ85=sQuery(id+"F0.wireOp",EDGE,"E4");var subQ86=sQuery(id+"F0.wireOp",EDGE,"E3");var subQ87=sQuery(id+"F0.wireOp",EDGE,"E2");var subQ88=sQuery(id+"F0.wireOp",EDGE,"E1");var subQ89=makeQuery(id+"F8.boolean.opBoolean","SPLIT",FACE,{"disambiguationData":[TD([subQ52])],"derivedFrom":makeQuery(id+"F6.boolean.opBoolean","MERGE",FACE,{"derivedFrom":[makeQuery(id+"F1.opExtrude","CAP_FACE",FACE,{"disambiguationData":[OSD([subQ25,subQ88,subQ87,subQ86,subQ85,subQ8,subQ43,subQ49,subQ55,subQ46,subQ41,subQ3,subQ84,subQ83,subQ82,subQ81,subQ80,subQ79,subQ78,subQ77,subQ76,subQ75,subQ74,subQ73,subQ7,subQ37,subQ6,subQ2,subQ72,subQ71,subQ70,subQ24,subQ69,subQ68,subQ67,subQ66,subQ65,subQ64,subQ63,subQ62,subQ61,subQ60,subQ59,subQ58,subQ57])],"isStart":true}),makeQuery(id+"F6.opExtrude","CAP_FACE",FACE,{"disambiguationData":[OSD([subQ25,subQ88,subQ87,subQ86,subQ85,subQ8,subQ43,subQ49,subQ55,subQ46,subQ41,subQ3,subQ84,subQ83,subQ82,subQ81,subQ80,subQ79,subQ78,subQ77,subQ76,subQ75,subQ74,subQ73,subQ7,subQ37,subQ6,subQ2,subQ72,subQ71,subQ70,subQ24,subQ69,subQ68,subQ67,subQ66,subQ65,subQ64,subQ63,subQ62,subQ61,subQ60,subQ59,subQ58,subQ57])],"isStart":false})]})});Q0=makeQuery(id+"F14.boolean.opBoolean","MERGE",FACE,{"derivedFrom":[makeQuery(id+"F12.opExtrude","SWEPT_FACE",FACE,{"disambiguationData":[OSD([subQ1])]}),makeQuery(id+"F13.boolean.opBoolean","MERGE",FACE,{"derivedFrom":[makeQuery(id+"F11.boolean.opBoolean","SPLIT",FACE,{"disambiguationData":[TD([subQ52])],"derivedFrom":subQ89}),makeQuery(id+"F12.boolean.opBoolean","MERGE",FACE,{"derivedFrom":[makeQuery(id+"F11.boolean.opBoolean","SPLIT",FACE,{"disambiguationData":[TD([subQ20])],"derivedFrom":subQ89}),makeQuery(id+"F12.opExtrude","SWEPT_FACE",FACE,{"disambiguationData":[OSD([subQ5])]})]}),makeQuery(id+"F13.opLoft","SWEPT_FACE",FACE,{"disambiguationData":[OSD([subQ8,subQ7,subQ6,sQuery(id+"F9.wireOp",EDGE,"E78"),sQuery(id+"F9.wireOp",EDGE,"E83"),subQ5,subQ4,sQuery(id+"F10.wireOp",EDGE,"E89.left"),sQuery(id+"F10.wireOp",EDGE,"E89.right")])]})]}),makeQuery(id+"F14.opLoft","SWEPT_FACE",FACE,{"disambiguationData":[OSD([subQ3,subQ2,sQuery(id+"F9.wireOp",EDGE,"E79"),sQuery(id+"F9.wireOp",EDGE,"E82"),subQ1,subQ0,sQuery(id+"F10.wireOp",EDGE,"E88.left"),sQuery(id+"F10.wireOp",EDGE,"E88.right")])]})]});}
            var sketch = newSketch(context, id + "F15", { "sketchPlane" : qUnion([Q0])});
            skLineSegment(sketch, "E90", {"start": v(-25.91, -72.77) * mm, "end": v(-25.91, -75.95) * mm});
            skPoint(sketch, "E90.startSnap0", {"position": v(-25.91, -79.37) * mm});
            skLineSegment(sketch, "E91", {"start": v(-25.91, -72.77) * mm, "end": v(-32.26, -72.77) * mm});
            skLineSegment(sketch, "E92", {"start": v(-32.26, -72.77) * mm, "end": v(-32.26, -98.17) * mm});
            skLineSegment(sketch, "E93", {"start": v(-25.91, -82.8) * mm, "end": v(-25.91, -84.4) * mm});
            skLineSegment(sketch, "E94", {"start": v(25.91, -72.77) * mm, "end": v(25.91, -75.95) * mm});
            skLineSegment(sketch, "E95", {"start": v(25.91, -75.95) * mm, "end": v(29.09, -75.95) * mm});
            skLineSegment(sketch, "E96", {"start": v(29.09, -75.95) * mm, "end": v(29.09, -82.8) * mm});
            skLineSegment(sketch, "E97", {"start": v(29.09, -82.8) * mm, "end": v(25.91, -82.8) * mm});
            skLineSegment(sketch, "E98", {"start": v(25.91, -82.8) * mm, "end": v(25.91, -84.4) * mm});
            skLineSegment(sketch, "E99", {"start": v(-25.91, -75.95) * mm, "end": v(-29.09, -75.95) * mm});
            skLineSegment(sketch, "E100", {"start": v(-29.09, -75.95) * mm, "end": v(-29.09, -82.8) * mm});
            skLineSegment(sketch, "E101", {"start": v(-29.09, -82.8) * mm, "end": v(-25.91, -82.8) * mm});
            skLineSegment(sketch, "E102", {"start": v(25.91, -72.77) * mm, "end": v(32.26, -72.77) * mm});
            skLineSegment(sketch, "E103", {"start": v(32.26, -72.77) * mm, "end": v(32.26, -98.17) * mm});
            skArc(sketch, "E104", {"start": v(-32.26, -98.17) * mm, "mid": v(0, -130.43) * mm, "end": v(32.26, -98.17) * mm});
            skArc(sketch, "E105", {"start": v(-29.09, -98.17) * mm, "mid": v(0, -127.26) * mm, "end": v(29.09, -98.17) * mm});
            skPoint(sketch, "E106", {"position": v(27.5, -82.8) * mm});
            skArc(sketch, "E107", {"start": v(-26.64, -87.57) * mm, "mid": v(-26.1, -86.02) * mm, "end": v(-25.91, -84.4) * mm});
            skArc(sketch, "E108", {"start": v(-26.64, -87.57) * mm, "mid": v(-28.47, -92.73) * mm, "end": v(-29.09, -98.17) * mm});
            skArc(sketch, "E109", {"start": v(25.91, -84.4) * mm, "mid": v(26.1, -86.02) * mm, "end": v(26.64, -87.57) * mm});
            skArc(sketch, "E110", {"start": v(29.09, -98.17) * mm, "mid": v(28.47, -92.73) * mm, "end": v(26.64, -87.57) * mm});
            skSolve(sketch);
        }
        {
            var Q0;
            Q0=makeQuery(id+"F15.imprint","IMPRINT",FACE,{"disambiguationData":[TD([[makeQuery(id+"F15.imprint","IMPRINT",EDGE,{"derivedFrom":sQuery(id+"F15.wireOp",EDGE,"E90")}),-1.0]])]});
            extrude(context, id + "F16", {"entities" : qUnion([Q0]), "depth" : 2.54 * mm, "hasSecondDirection" : true, "secondDirectionOppositeDirection" : true, "secondDirectionDepth" : 15.24 * mm});
        }
        {
            var Q0;
            Q0=makeQuery(id+"F16.opExtrude","SWEPT_FACE",FACE,{"disambiguationData":[OSD([sQuery(id+"F15.wireOp",EDGE,"E95")])]});
            var sketch = newSketch(context, id + "F17", { "sketchPlane" : qUnion([Q0])});
            skLineSegment(sketch, "E111.0", {"start": v(-28.58, 9.52) * mm, "end": v(-25.91, 12.7) * mm});
            skLineSegment(sketch, "E112", {"start": v(-25.91, 13.1) * mm, "end": v(-29.09, 9.31) * mm});
            skLineSegment(sketch, "E113.0", {"start": v(-25.91, 0) * mm, "end": v(-28.58, 3.18) * mm});
            skLineSegment(sketch, "E114", {"start": v(-25.91, -0.4) * mm, "end": v(-29.09, 3.39) * mm});
            skSolve(sketch);
        }
        {
            var Q0;
            {var subQ0=sQuery(id+"F17.wireOp",EDGE,"E114");Q0=makeQuery(id+"F17.imprint","IMPRINT",FACE,{"disambiguationData":[TD([[makeQuery(id+"F17.imprint","IMPRINT",EDGE,{"derivedFrom":subQ0}),1.0]])]});}
            var Q1;
            {var subQ0=sQuery(id+"F17.wireOp",EDGE,"E112");Q1=makeQuery(id+"F17.imprint","IMPRINT",FACE,{"disambiguationData":[TD([[makeQuery(id+"F17.imprint","IMPRINT",EDGE,{"derivedFrom":subQ0}),-1.0]])]});}
            var Q2;
            Q2=makeQuery(id+"F16.opExtrude","SWEPT_FACE",FACE,{"disambiguationData":[OSD([sQuery(id+"F15.wireOp",EDGE,"E97")])]});
            extrude(context, id + "F18", {"entities" : qUnion([Q0, Q1]), "operationType" : NewBodyOperationType.ADD, "endBound" : BoundingType.UP_TO_SURFACE, "endBoundEntityFace" : qUnion([Q2]), "depth" : 25.4 * mm});
        }
        {
            var Q0;
            Q0=makeQuery(id+"F16.opExtrude","SWEPT_BODY",BODY,{"disambiguationData":[OSD([sQuery(id+"F15.wireOp",EDGE,"E90"),sQuery(id+"F15.wireOp",EDGE,"E91"),sQuery(id+"F15.wireOp",EDGE,"E92"),sQuery(id+"F15.wireOp",EDGE,"E93"),sQuery(id+"F15.wireOp",EDGE,"E94"),sQuery(id+"F15.wireOp",EDGE,"E95"),sQuery(id+"F15.wireOp",EDGE,"E96"),sQuery(id+"F15.wireOp",EDGE,"E97"),sQuery(id+"F15.wireOp",EDGE,"E98"),sQuery(id+"F15.wireOp",EDGE,"E99"),sQuery(id+"F15.wireOp",EDGE,"E100"),sQuery(id+"F15.wireOp",EDGE,"E101"),sQuery(id+"F15.wireOp",EDGE,"E102"),sQuery(id+"F15.wireOp",EDGE,"E103"),sQuery(id+"F15.wireOp",EDGE,"E104"),sQuery(id+"F15.wireOp",EDGE,"E105"),sQuery(id+"F15.wireOp",EDGE,"E107"),sQuery(id+"F15.wireOp",EDGE,"E108"),sQuery(id+"F15.wireOp",EDGE,"E109"),sQuery(id+"F15.wireOp",EDGE,"E110")])]});
            var Q1;
            Q1=qCreatedBy(makeId("Right.planeOp"),FACE);
            mirror(context, id + "F19", {"operationType" : NewBodyOperationType.ADD, "entities" : qUnion([Q0]), "mirrorPlane" : qUnion([Q1])});
        }
        {
            var Q0;
            Q0=makeQuery(id+"F1.opExtrude","SWEPT_FACE",FACE,{"disambiguationData":[OSD([sQuery(id+"F0.wireOp",EDGE,"E1")])]});
            var sketch = newSketch(context, id + "F20", { "sketchPlane" : qUnion([Q0])});
            skLineSegment(sketch, "E115.bottom", {"start": v(76.2, 8.9) * mm, "end": v(85.73, 8.9) * mm});
            skLineSegment(sketch, "E115.top", {"start": v(76.2, 3.81) * mm, "end": v(85.73, 3.81) * mm});
            skLineSegment(sketch, "E115.left", {"start": v(76.2, 8.9) * mm, "end": v(76.2, 3.81) * mm});
            skLineSegment(sketch, "E115.right", {"start": v(85.73, 8.9) * mm, "end": v(85.73, 3.81) * mm});
            skLineSegment(sketch, "E116", {"start": v(85.73, 12.7) * mm, "end": v(85.73, 0) * mm});
            skSolve(sketch);
        }
        {
            var Q0;
            {var subQ0=sQuery(id+"F20.wireOp",EDGE,"E115.bottom");Q0=makeQuery(id+"F20.imprint","IMPRINT",FACE,{"disambiguationData":[TD([[makeQuery(id+"F20.imprint","IMPRINT",EDGE,{"derivedFrom":subQ0}),-1.0]])]});}
            extrude(context, id + "F21", {"entities" : qUnion([Q0]), "operationType" : NewBodyOperationType.REMOVE, "oppositeDirection" : true, "depth" : 25.4 * mm});
        }
        {
            var Q0;
            Q0=makeQuery(id+"F1.opExtrude","SWEPT_FACE",FACE,{"disambiguationData":[OSD([sQuery(id+"F0.wireOp",EDGE,"E42.MirrorCS")])]});
            var sketch = newSketch(context, id + "F22", { "sketchPlane" : qUnion([Q0])});
            skLineSegment(sketch, "E117.0", {"start": v(-76.2, 8.9) * mm, "end": v(-76.2, 3.81) * mm});
            skLineSegment(sketch, "E118.0", {"start": v(-85.73, 8.9) * mm, "end": v(-76.2, 8.9) * mm});
            skLineSegment(sketch, "E119.0", {"start": v(-85.73, 3.81) * mm, "end": v(-76.2, 3.81) * mm});
            skLineSegment(sketch, "E120", {"start": v(-85.73, 3.81) * mm, "end": v(-85.73, 8.9) * mm});
            skSolve(sketch);
        }
        {
            var Q0;
            Q0=makeQuery(id+"F22.imprint","IMPRINT",FACE,{"disambiguationData":[TD([[makeQuery(id+"F22.imprint","IMPRINT",EDGE,{"derivedFrom":sQuery(id+"F22.wireOp",EDGE,"E117.0")}),-1.0]])]});
            extrude(context, id + "F23", {"entities" : qUnion([Q0]), "operationType" : NewBodyOperationType.REMOVE, "oppositeDirection" : true, "depth" : 25.4 * mm});
        }
        {
            var Q0;
            Q0=makeQuery(id+"F12.opExtrude","SWEPT_FACE",FACE,{"disambiguationData":[OSD([sQuery(id+"F9.wireOp",EDGE,"E78")])]});
            var sketch = newSketch(context, id + "F24", { "sketchPlane" : qUnion([Q0])});
            skArc(sketch, "E121", {"start": v(-19.05, 21.32) * mm, "mid": v(-24.15, 4.86) * mm, "end": v(-19.05, -11.59) * mm});
            skLineSegment(sketch, "E122.0.0", {"start": v(-19.05, 5) * mm, "end": v(-19.05, -11.59) * mm});
            skLineSegment(sketch, "E122.0.1", {"start": v(-19.05, -11.59) * mm, "end": v(-31.75, -11.59) * mm});
            skLineSegment(sketch, "E122.0.2", {"start": v(-31.75, -11.59) * mm, "end": v(-31.75, 5) * mm});
            skLineSegment(sketch, "E122.0.3", {"start": v(-31.75, 5) * mm, "end": v(-19.05, 5) * mm});
            skSolve(sketch);
        }
        {
            var Q0;
            {var subQ0=sQuery(id+"F24.wireOp",EDGE,"E121");var subQ4=sQuery(id+"F24.wireOp",EDGE,"E122.0.3");var subQ5=makeQuery(id+"F24.imprint","INTERSECT",VERTEX,{"derivedFrom":[subQ0,subQ4]});Q0=makeQuery(id+"F24.imprint","IMPRINT",FACE,{"disambiguationData":[TD([[makeQuery(id+"F24.imprint","IMPRINT",EDGE,{"disambiguationData":[TD([[subQ5,-1.0]])],"derivedFrom":subQ4}),1.0]])]});}
            var Q1;
            {var subQ0=sQuery(id+"F24.wireOp",EDGE,"E122.0.0");var subQ1=sQuery(id+"F24.wireOp",EDGE,"E121");var subQ2=makeQuery(id+"F24.imprint","INTERSECT",VERTEX,{"derivedFrom":[subQ1,subQ0,sQuery(id+"F24.wireOp",EDGE,"E122.0.1")]});Q1=makeQuery(id+"F24.imprint","IMPRINT",FACE,{"disambiguationData":[TD([[makeQuery(id+"F24.imprint","IMPRINT",EDGE,{"disambiguationData":[TD([[subQ2,1.0]])],"derivedFrom":subQ1}),1.0]])]});}
            var Q2;
            {var subQ0=sQuery(id+"F24.wireOp",EDGE,"E122.0.3");var subQ1=sQuery(id+"F24.wireOp",EDGE,"E121");var subQ2=makeQuery(id+"F24.imprint","INTERSECT",VERTEX,{"derivedFrom":[subQ1,subQ0]});Q2=makeQuery(id+"F24.imprint","IMPRINT",FACE,{"disambiguationData":[TD([[makeQuery(id+"F24.imprint","IMPRINT",EDGE,{"disambiguationData":[TD([[subQ2,-1.0]])],"derivedFrom":subQ0}),-1.0]])]});}
            var Q3;
            Q3=makeQuery(id+"F12.opExtrude","SWEPT_FACE",FACE,{"disambiguationData":[OSD([sQuery(id+"F9.wireOp",EDGE,"E79")])]});
            extrude(context, id + "F25", {"entities" : qUnion([Q0, Q1, Q2]), "operationType" : NewBodyOperationType.ADD, "endBound" : BoundingType.UP_TO_SURFACE, "endBoundEntityFace" : qUnion([Q3]), "depth" : 25.4 * mm});
        }
        {
            var Q0;
            Q0=makeQuery(id+"F6.opExtrude","SWEPT_FACE",FACE,{"disambiguationData":[OSD([sQuery(id+"F5.wireOp",EDGE,"E45.left")])]});
            var sketch = newSketch(context, id + "F26", { "sketchPlane" : qUnion([Q0])});
            skEllipticalArc(sketch, "E123.0", {});
            skEllipticalArc(sketch, "E124.0", {});
            skLineSegment(sketch, "E125.0", {"start": v(-19.05, 12.7) * mm, "end": v(-19.05, 25.2) * mm});
            skLineSegment(sketch, "E126.0", {"start": v(-19.05, 0) * mm, "end": v(-19.05, -12.5) * mm});
            skLineSegment(sketch, "E127.0", {"start": v(-24.15, 12.7) * mm, "end": v(-19.05, 12.7) * mm});
            skLineSegment(sketch, "E128.0", {"start": v(-24.15, 0) * mm, "end": v(-19.05, 0) * mm});
            const initialGuessF26  = {"E123.0": [0.004934912315530384, 9.647076837248584e-05, 1, 0, 0.029085540000000003, 0.02228081629211476, 3.1459224352518027, 3.742834892766333], "E124.0": [0.004934912315530383, 0.012603529231625998, 1, 0, 0.029085540000000003, 0.022280816292114758, 2.540350414414236, 3.137262871929641]};
            skSetInitialGuess(sketch, initialGuessF26);
            skSolve(sketch);
        }
        {
            var Q0;
            Q0=makeQuery(id+"F26.imprint","IMPRINT",FACE,{"disambiguationData":[TD([[makeQuery(id+"F26.imprint","IMPRINT",EDGE,{"derivedFrom":sQuery(id+"F26.wireOp",EDGE,"E124.0")}),1.0]])]});
            var Q1;
            Q1=makeQuery(id+"F26.imprint","IMPRINT",FACE,{"disambiguationData":[TD([[makeQuery(id+"F26.imprint","IMPRINT",EDGE,{"derivedFrom":sQuery(id+"F26.wireOp",EDGE,"E123.0")}),1.0]])]});
            var Q2;
            Q2=makeQuery(id+"F6.opExtrude","SWEPT_FACE",FACE,{"disambiguationData":[OSD([sQuery(id+"F5.wireOp",EDGE,"E46.left")])]});
            extrude(context, id + "F27", {"entities" : qUnion([Q0, Q1]), "operationType" : NewBodyOperationType.REMOVE, "endBound" : BoundingType.UP_TO_SURFACE, "oppositeDirection" : true, "endBoundEntityFace" : qUnion([Q2]), "depth" : 25.4 * mm});
        }
    });
